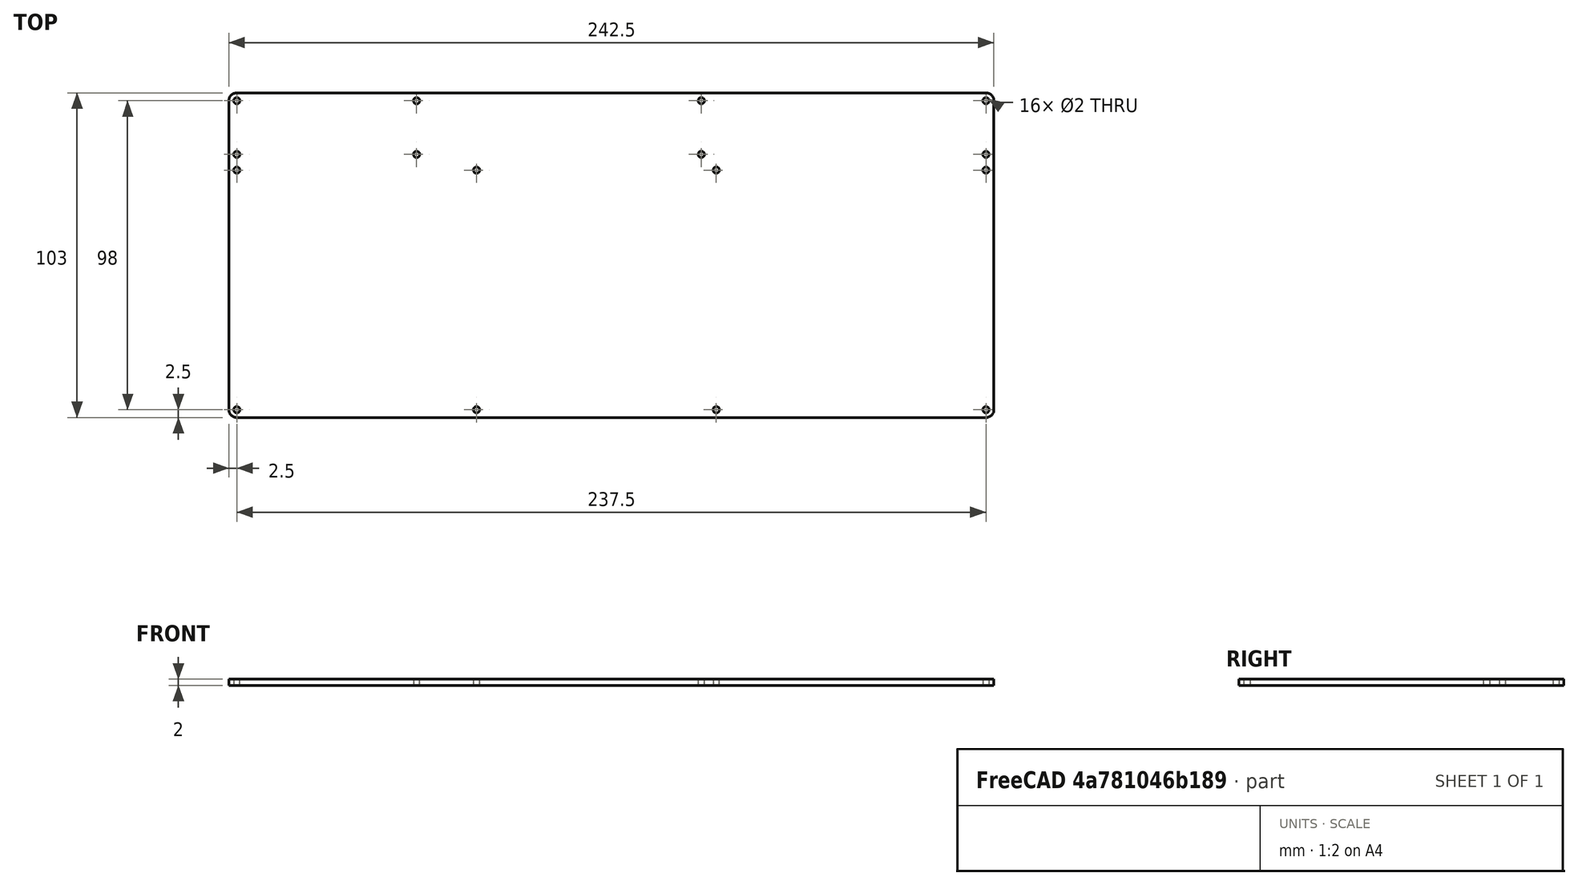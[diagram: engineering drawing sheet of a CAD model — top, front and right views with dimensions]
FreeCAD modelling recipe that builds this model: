
FCSTD DOCUMENT  (FreeCAD 1.0R39285 (Git))
Label: bottom-plate
License: All rights reserved
LicenseURL: https://en.wikipedia.org/wiki/All_rights_reserved
objects: Sketcher::SketchObject×2, PartDesign::Pad×1, PartDesign::Body×1
note: 8 computed .brp shape members not serialized (recipe doc carries the construction recipe); baked Part::Feature solids carry a one-line shape summary decoded from their .brp

FEATURE [Sketcher::SketchObject] Sketch
  ArcFitTolerance = 1e-06
  FullyConstrained = true
  MakeInternals = false
FEATURE [Sketcher::SketchObject] Sketch001
  ArcFitTolerance = 1e-06
  AttachmentSupport = -> [XY_Plane]
  FullyConstrained = true
  MakeInternals = false
  MapMode = 5
  sketch-geometry (24):
    g0: LineSegment StartX=-121.25 StartY=-49 StartZ=0 EndX=-121.25 EndY=49 EndZ=0
    g1: ArcOfCircle CenterX=-118.75 CenterY=49 CenterZ=0 NormalX=0 NormalY=0 NormalZ=1 AngleXU=0 Radius=2.5 StartAngle=1.5708 EndAngle=3.14159
    g2: LineSegment StartX=-118.75 StartY=51.5 StartZ=0 EndX=118.75 EndY=51.5 EndZ=0
    g3: ArcOfCircle CenterX=118.75 CenterY=49 CenterZ=0 NormalX=0 NormalY=0 NormalZ=1 AngleXU=0 Radius=2.5 StartAngle=1e-16 EndAngle=1.5708
    g4: LineSegment StartX=121.25 StartY=49 StartZ=0 EndX=121.25 EndY=-49 EndZ=0
    g5: ArcOfCircle CenterX=118.75 CenterY=-49 CenterZ=0 NormalX=0 NormalY=0 NormalZ=1 AngleXU=0 Radius=2.5 StartAngle=4.71239 EndAngle=6.28319
    g6: LineSegment StartX=118.75 StartY=-51.5 StartZ=0 EndX=-118.75 EndY=-51.5 EndZ=0
    g7: ArcOfCircle CenterX=-118.75 CenterY=-49 CenterZ=0 NormalX=0 NormalY=0 NormalZ=1 AngleXU=0 Radius=2.5 StartAngle=3.14159 EndAngle=4.71239
    g8: Circle CenterX=-118.75 CenterY=49 CenterZ=0 NormalX=0 NormalY=0 NormalZ=1 AngleXU=0 Radius=1
    g9: Circle CenterX=-61.75 CenterY=49 CenterZ=0 NormalX=0 NormalY=0 NormalZ=1 AngleXU=0 Radius=1
    g10: Circle CenterX=28.5 CenterY=49 CenterZ=0 NormalX=0 NormalY=0 NormalZ=1 AngleXU=0 Radius=1
    g11: Circle CenterX=118.75 CenterY=49 CenterZ=0 NormalX=0 NormalY=0 NormalZ=1 AngleXU=0 Radius=1
    g12: Circle CenterX=-118.75 CenterY=32 CenterZ=0 NormalX=0 NormalY=0 NormalZ=1 AngleXU=0 Radius=1
    g13: Circle CenterX=-61.75 CenterY=32 CenterZ=0 NormalX=0 NormalY=0 NormalZ=1 AngleXU=0 Radius=1
    g14: Circle CenterX=28.5 CenterY=32 CenterZ=0 NormalX=0 NormalY=0 NormalZ=1 AngleXU=0 Radius=1
    g15: Circle CenterX=118.75 CenterY=32 CenterZ=0 NormalX=0 NormalY=0 NormalZ=1 AngleXU=0 Radius=1
    g16: Circle CenterX=-118.75 CenterY=27 CenterZ=0 NormalX=0 NormalY=0 NormalZ=1 AngleXU=0 Radius=1
    g17: Circle CenterX=-42.75 CenterY=27 CenterZ=0 NormalX=0 NormalY=0 NormalZ=1 AngleXU=0 Radius=1
    g18: Circle CenterX=33.25 CenterY=27 CenterZ=0 NormalX=0 NormalY=0 NormalZ=1 AngleXU=0 Radius=1
    g19: Circle CenterX=118.75 CenterY=27 CenterZ=0 NormalX=0 NormalY=0 NormalZ=1 AngleXU=0 Radius=1
    g20: Circle CenterX=-118.75 CenterY=-49 CenterZ=0 NormalX=0 NormalY=0 NormalZ=1 AngleXU=0 Radius=1
    g21: Circle CenterX=-42.75 CenterY=-49 CenterZ=0 NormalX=0 NormalY=0 NormalZ=1 AngleXU=0 Radius=1
    g22: Circle CenterX=33.25 CenterY=-49 CenterZ=0 NormalX=0 NormalY=0 NormalZ=1 AngleXU=0 Radius=1
    g23: Circle CenterX=118.75 CenterY=-49 CenterZ=0 NormalX=0 NormalY=0 NormalZ=1 AngleXU=0 Radius=1
  constraints (67):
    c: Tangent(g0,g1) = 1.5708
    c: Tangent(g1,g2) = 1.5708
    c: Tangent(g2,g3) = 1.5708
    c: Tangent(g3,g4) = 1.5708
    c: Tangent(g4,g5) = 1.5708
    c: Tangent(g5,g6) = 1.5708
    c: Tangent(g6,g7) = 1.5708
    c: Tangent(g7,g0) = 1.5708
    c: Vertical(g0)
    c: Vertical(g4)
    c: Horizontal(g2)
    c: Horizontal(g6)
    c: Radius(g1) = 2.5
    c: Radius(g3) = 2.5
    c: Radius(g5) = 2.5
    c: Radius(g7) = 2.5
    c: Symmetric(g1,g5,g-1)
    c: Distance(g4,g0) = 242.5
    c: Distance(g6,g2) = 103
    c: Diameter(g8) = 2
    c: Diameter(g9) = 2
    c: Diameter(g10) = 2
    c: Diameter(g11) = 2
    c: Diameter(g12) = 2
    c: Diameter(g13) = 2
    c: Diameter(g14) = 2
    c: Diameter(g15) = 2
    c: Diameter(g16) = 2
    c: Diameter(g17) = 2
    c: Diameter(g18) = 2
    c: Diameter(g19) = 2
    c: Diameter(g20) = 2
    c: Diameter(g21) = 2
    c: Diameter(g22) = 2
    c: Diameter(g23) = 2
    c: Distance(g8,g2) = 2.5
    c: Distance(g8,g0) = 2.5
    c: Distance(g20,g0) = 2.5
    c: Distance(g20,g6) = 2.5
    c: Distance(g23,g4) = 2.5
    c: Distance(g11,g4) = 2.5
    c: Distance(g9,g0) = 59.5
    c: Distance(g12,g2) = 19.5
    c: Horizontal(g1,g9)
    c: Horizontal(g9,g10)
    c: Horizontal(g10,g11)
    c: Vertical(g1,g12)
    c: Vertical(g13,g9)
    c: Horizontal(g12,g13)
    c: Distance(g10,g4) = 92.75
    c: Vertical(g3,g15)
    c: Horizontal(g15,g13)
    c: Horizontal(g13,g14)
    c: Horizontal(g7,g21)
    c: Horizontal(g21,g22)
    c: Horizontal(g23,g22)
    c: Vertical(g19,g5)
    c: Vertical(g7,g16)
    c: Distance(g16,g6) = 78.5
    c: Vertical(g17,g21)
    c: Horizontal(g16,g17)
    c: Horizontal(g18,g17)
    c: Horizontal(g19,g18)
    c: Vertical(g18,g22)
    c: Distance(g22,g4) = 88
    c: Vertical(g10,g14)
    c: Distance(g21,g0) = 78.5  'h0l1_14_h'
FEATURE [PartDesign::Pad] Pad
  Direction = (0,0,1)
  Length = 2
  Length2 = 10
  Profile = -> Sketch001
  ReferenceAxis = -> Sketch001 [N_Axis]
  Refine = true
  Suppressed = false
  Type = 0
FEATURE [PartDesign::Body] Body
  AllowCompound = false
  Group = -> [Sketch001,Pad]
  Origin = -> Origin
  Tip = -> Pad
